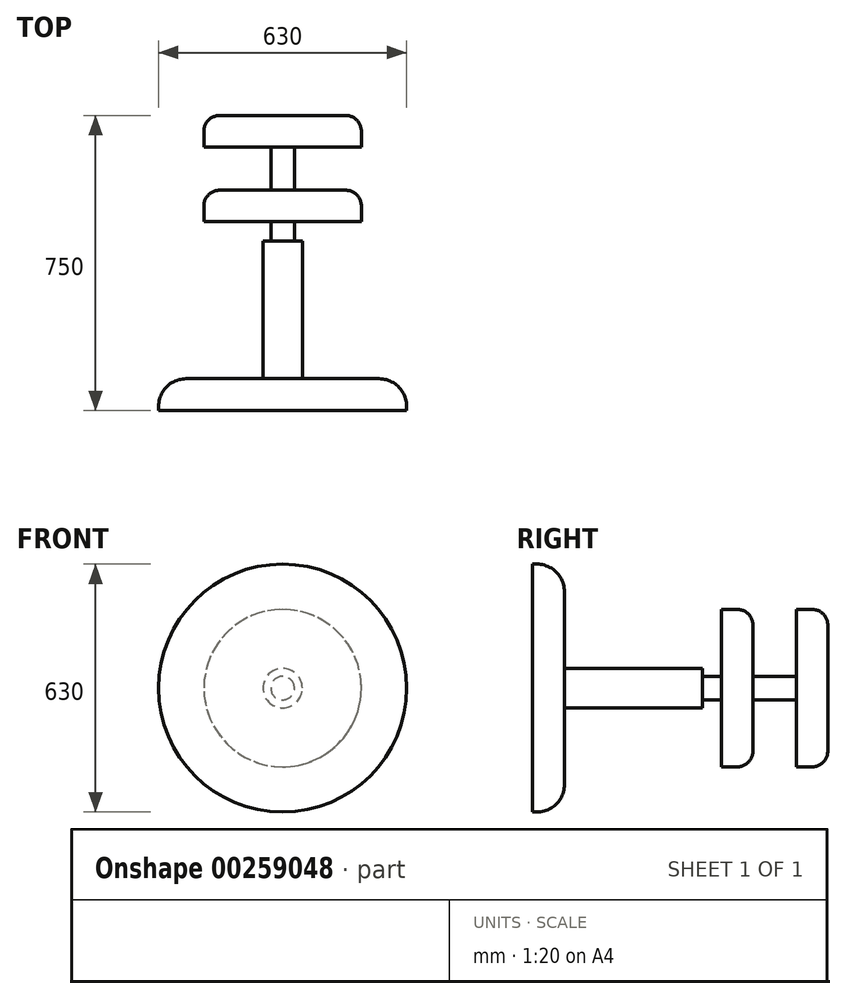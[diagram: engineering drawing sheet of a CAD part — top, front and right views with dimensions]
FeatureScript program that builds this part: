
annotation { "Feature Type Name" : "Feature", "Feature Type Description" : "" }
export const myFeature = defineFeature(function(context is Context, id is Id, definition is map)
    precondition{}
    {
        {
            var Q0;
            Q0=qCreatedBy(makeId("Top.planeOp"),FACE);
            var sketch = newSketch(context, id + "F0", { "sketchPlane" : qUnion([Q0])});
            skLineSegment(sketch, "E0.bottom", {"start": v(-315, 0) * mm, "end": v(315, 0) * mm});
            skLineSegment(sketch, "E0.top", {"start": v(-315, 81.08) * mm, "end": v(315, 81.08) * mm});
            skLineSegment(sketch, "E0.left", {"start": v(-315, 0) * mm, "end": v(-315, 81.08) * mm});
            skLineSegment(sketch, "E0.right", {"start": v(315, 0) * mm, "end": v(315, 81.08) * mm});
            skLineSegment(sketch, "E1.bottom", {"start": v(-200, 560) * mm, "end": v(200, 560) * mm});
            skLineSegment(sketch, "E1.top", {"start": v(-200, 480) * mm, "end": v(200, 480) * mm});
            skLineSegment(sketch, "E1.left", {"start": v(-200, 560) * mm, "end": v(-200, 480) * mm});
            skLineSegment(sketch, "E1.right", {"start": v(200, 560) * mm, "end": v(200, 480) * mm});
            skLineSegment(sketch, "E2.bottom", {"start": v(-200, 750) * mm, "end": v(200, 750) * mm});
            skLineSegment(sketch, "E2.top", {"start": v(-200, 670) * mm, "end": v(200, 670) * mm});
            skLineSegment(sketch, "E2.left", {"start": v(-200, 750) * mm, "end": v(-200, 670) * mm});
            skLineSegment(sketch, "E2.right", {"start": v(200, 750) * mm, "end": v(200, 670) * mm});
            skLineSegment(sketch, "E3", {"start": v(0, 0) * mm, "end": v(0, 1180.73) * mm, "construction": true});
            skLineSegment(sketch, "E4.bottom", {"start": v(-50, 81.08) * mm, "end": v(50, 81.08) * mm});
            skLineSegment(sketch, "E4.top", {"start": v(-50, 431.08) * mm, "end": v(50, 431.08) * mm});
            skLineSegment(sketch, "E4.left", {"start": v(-50, 81.08) * mm, "end": v(-50, 431.08) * mm});
            skLineSegment(sketch, "E4.right", {"start": v(50, 81.08) * mm, "end": v(50, 431.08) * mm});
            skLineSegment(sketch, "E5.bottom", {"start": v(-30, 431.08) * mm, "end": v(30, 431.08) * mm});
            skLineSegment(sketch, "E5.top", {"start": v(-30, 480) * mm, "end": v(30, 480) * mm});
            skLineSegment(sketch, "E5.left", {"start": v(-30, 431.08) * mm, "end": v(-30, 480) * mm});
            skLineSegment(sketch, "E5.right", {"start": v(30, 431.08) * mm, "end": v(30, 480) * mm});
            skLineSegment(sketch, "E6.top", {"start": v(-30, 670) * mm, "end": v(30, 670) * mm});
            skLineSegment(sketch, "E6.left", {"start": v(-30, 431.08) * mm, "end": v(-30, 670) * mm});
            skLineSegment(sketch, "E6.right", {"start": v(30, 431.08) * mm, "end": v(30, 670) * mm});
            skLineSegment(sketch, "E7", {"start": v(0, 750) * mm, "end": v(0, 0) * mm});
            skSolve(sketch);
        }
        {
            var Q0;
            {var subQ0=sQuery(id+"F0.wireOp",EDGE,"E2.left");Q0=makeQuery(id+"F0.imprint","IMPRINT",FACE,{"disambiguationData":[TD([[makeQuery(id+"F0.imprint","IMPRINT",EDGE,{"derivedFrom":subQ0}),1.0]])]});}
            var Q1;
            {var subQ0=sQuery(id+"F0.wireOp",EDGE,"E6.left");var subQ1=sQuery(id+"F0.wireOp",EDGE,"E1.bottom");var subQ2=makeQuery(id+"F0.imprint","INTERSECT",VERTEX,{"derivedFrom":[subQ1,subQ0]});Q1=makeQuery(id+"F0.imprint","IMPRINT",FACE,{"disambiguationData":[TD([[makeQuery(id+"F0.imprint","IMPRINT",EDGE,{"disambiguationData":[TD([[subQ2,-1.0]])],"derivedFrom":subQ1}),1.0]])]});}
            var Q2;
            {var subQ0=sQuery(id+"F0.wireOp",EDGE,"E6.left");var subQ1=sQuery(id+"F0.wireOp",EDGE,"E1.bottom");var subQ2=makeQuery(id+"F0.imprint","INTERSECT",VERTEX,{"derivedFrom":[subQ1,subQ0]});Q2=makeQuery(id+"F0.imprint","IMPRINT",FACE,{"disambiguationData":[TD([[makeQuery(id+"F0.imprint","IMPRINT",EDGE,{"disambiguationData":[TD([[subQ2,-1.0]])],"derivedFrom":subQ1}),-1.0]])]});}
            var Q3;
            {var subQ1=sQuery(id+"F0.wireOp",EDGE,"E5.top");var subQ3=sQuery(id+"F0.wireOp",EDGE,"E7");var subQ4=makeQuery(id+"F0.imprint","INTERSECT",VERTEX,{"derivedFrom":[subQ1,subQ3]});Q3=makeQuery(id+"F0.imprint","IMPRINT",FACE,{"disambiguationData":[TD([[makeQuery(id+"F0.imprint","IMPRINT",EDGE,{"disambiguationData":[TD([[subQ4,-1.0]])],"derivedFrom":subQ3}),-1.0]])]});}
            var Q4;
            {var subQ0=sQuery(id+"F0.wireOp",EDGE,"E1.left");Q4=makeQuery(id+"F0.imprint","IMPRINT",FACE,{"disambiguationData":[TD([[makeQuery(id+"F0.imprint","IMPRINT",EDGE,{"derivedFrom":subQ0}),1.0]])]});}
            var Q5;
            {var subQ5=sQuery(id+"F0.wireOp",EDGE,"E4.left");Q5=makeQuery(id+"F0.imprint","IMPRINT",FACE,{"disambiguationData":[TD([[makeQuery(id+"F0.imprint","IMPRINT",EDGE,{"derivedFrom":subQ5}),-1.0]])]});}
            var Q6;
            {var subQ5=sQuery(id+"F0.wireOp",EDGE,"E0.left");Q6=makeQuery(id+"F0.imprint","IMPRINT",FACE,{"disambiguationData":[TD([[makeQuery(id+"F0.imprint","IMPRINT",EDGE,{"derivedFrom":subQ5}),-1.0]])]});}
            var Q7;
            Q7=sQuery(id+"F0.wireOp",EDGE,"E3");
            revolve(context, id + "F1", {"entities" : qUnion([Q0, Q1, Q2, Q3, Q4, Q5, Q6]), "axis" : qUnion([Q7]), "revolveType" : RevolveType.FULL});
        }
        {
            var Q0;
            Q0=makeQuery(id+"F1.opRevolve","SWEPT_EDGE",EDGE,{"disambiguationData":[OSD([sQuery(id+"F0.wireOp",EDGE,"E2.bottom"),sQuery(id+"F0.wireOp",EDGE,"E2.left")])]});
            fillet(context, id + "F2", {"entities" : qUnion([Q0]), "radius" : 40 * mm, "tangentPropagation" : true, "allowEdgeOverflow" : false});
        }
        {
            var Q0;
            Q0=makeQuery(id+"F1.opRevolve","SWEPT_EDGE",EDGE,{"disambiguationData":[OSD([sQuery(id+"F0.wireOp",EDGE,"E1.bottom"),sQuery(id+"F0.wireOp",EDGE,"E1.left")])]});
            fillet(context, id + "F3", {"entities" : qUnion([Q0]), "radius" : 40 * mm, "tangentPropagation" : true, "allowEdgeOverflow" : false});
        }
        {
            var Q0;
            Q0=makeQuery(id+"F1.opRevolve","SWEPT_EDGE",EDGE,{"disambiguationData":[OSD([sQuery(id+"F0.wireOp",EDGE,"E0.top"),sQuery(id+"F0.wireOp",EDGE,"E0.left")])]});
            fillet(context, id + "F4", {"entities" : qUnion([Q0]), "radius" : 70 * mm, "tangentPropagation" : true, "allowEdgeOverflow" : false});
        }
    });
